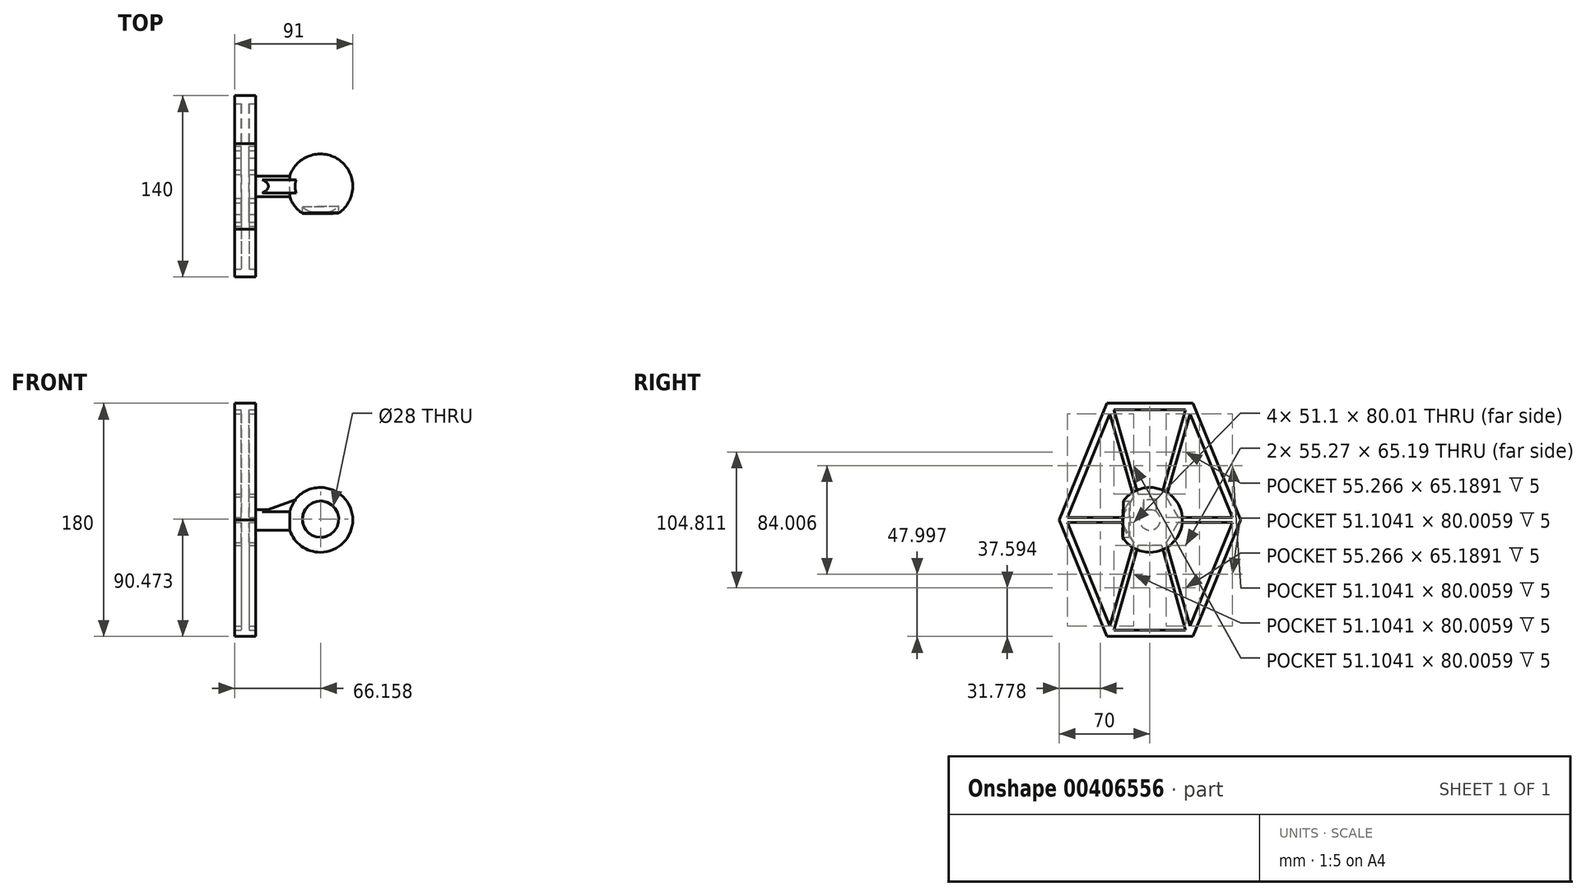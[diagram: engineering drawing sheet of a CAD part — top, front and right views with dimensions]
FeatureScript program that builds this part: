
annotation { "Feature Type Name" : "Feature", "Feature Type Description" : "" }
export const myFeature = defineFeature(function(context is Context, id is Id, definition is map)
    precondition{}
    {
        {
            var Q0;
            Q0=qCreatedBy(makeId("Front.planeOp"),FACE);
            var sketch = newSketch(context, id + "F0", { "sketchPlane" : qUnion([Q0])});
            skArc(sketch, "E0", {"start": v(0, -25) * mm, "mid": v(25, 0) * mm, "end": v(0, 25) * mm});
            skLineSegment(sketch, "E1", {"start": v(0, 25) * mm, "end": v(0, -25) * mm});
            skSolve(sketch);
        }
        {
            var Q0;
            Q0=qSketchRegion(id+"F0",true);
            var Q1;
            Q1=sQuery(id+"F0.wireOp",EDGE,"E1");
            revolve(context, id + "F1", {"entities" : qUnion([Q0]), "axis" : qUnion([Q1]), "revolveType" : RevolveType.FULL});
        }
        {
            var Q0;
            Q0=qCreatedBy(makeId("Front.planeOp"),FACE);
            var sketch = newSketch(context, id + "F2", { "sketchPlane" : qUnion([Q0])});
            skLineSegment(sketch, "E2.bottom", {"start": v(0, 0) * mm, "end": v(-55, 0) * mm});
            skLineSegment(sketch, "E2.top", {"start": v(0, 8) * mm, "end": v(-55, 8) * mm});
            skLineSegment(sketch, "E2.left", {"start": v(0, 0) * mm, "end": v(0, 8) * mm});
            skLineSegment(sketch, "E2.right", {"start": v(-55, 0) * mm, "end": v(-55, 8) * mm});
            skSolve(sketch);
        }
        {
            var Q0;
            Q0=qSketchRegion(id+"F2",true);
            var Q1;
            Q1=sQuery(id+"F2.wireOp",EDGE,"E2.bottom");
            revolve(context, id + "F3", {"operationType" : NewBodyOperationType.ADD, "entities" : qUnion([Q0]), "axis" : qUnion([Q1]), "revolveType" : RevolveType.FULL});
        }
        {
            var Q0;
            Q0=makeQuery(id+"F3.opRevolve","SWEPT_FACE",FACE,{"disambiguationData":[OSD([sQuery(id+"F2.wireOp",EDGE,"E2.right")])]});
            var sketch = newSketch(context, id + "F4", { "sketchPlane" : qUnion([Q0])});
            skLineSegment(sketch, "E3", {"start": v(0, 90) * mm, "end": v(-33.06, 90) * mm});
            skLineSegment(sketch, "E4", {"start": v(-33.06, 90) * mm, "end": v(-70, 0) * mm});
            skLineSegment(sketch, "E5", {"start": v(-70, 0) * mm, "end": v(0, 0) * mm, "construction": true});
            skLineSegment(sketch, "E6", {"start": v(0, 0) * mm, "end": v(0, 90) * mm, "construction": true});
            skLineSegment(sketch, "E7.MirrorCS", {"start": v(-33.06, -90) * mm, "end": v(-70, 0) * mm});
            skLineSegment(sketch, "E8.MirrorCS", {"start": v(0, -90) * mm, "end": v(-33.06, -90) * mm});
            skLineSegment(sketch, "E9.MirrorCS", {"start": v(0, 90) * mm, "end": v(33.06, 90) * mm});
            skLineSegment(sketch, "E10.MirrorCS", {"start": v(33.06, 90) * mm, "end": v(70, 0) * mm});
            skLineSegment(sketch, "E11.MirrorCS", {"start": v(33.06, -90) * mm, "end": v(70, 0) * mm});
            skLineSegment(sketch, "E12.MirrorCS", {"start": v(0, -90) * mm, "end": v(33.06, -90) * mm});
            skSolve(sketch);
        }
        {
            var Q0;
            Q0=qSketchRegion(id+"F4",true);
            extrude(context, id + "F5", {"entities" : qUnion([Q0]), "operationType" : NewBodyOperationType.ADD, "depth" : 6 * mm});
        }
        {
            var Q0;
            Q0=makeQuery(id+"F5.opExtrude","CAP_FACE",FACE,{"disambiguationData":[OSD([sQuery(id+"F4.wireOp",EDGE,"E3"),sQuery(id+"F4.wireOp",EDGE,"E4"),sQuery(id+"F4.wireOp",EDGE,"E7.MirrorCS"),sQuery(id+"F4.wireOp",EDGE,"E8.MirrorCS"),sQuery(id+"F4.wireOp",EDGE,"E9.MirrorCS"),sQuery(id+"F4.wireOp",EDGE,"E10.MirrorCS"),sQuery(id+"F4.wireOp",EDGE,"E11.MirrorCS"),sQuery(id+"F4.wireOp",EDGE,"E12.MirrorCS")])],"isStart":false});
            var sketch = newSketch(context, id + "F6", { "sketchPlane" : qUnion([Q0])});
            skLineSegment(sketch, "E13.0", {"start": v(-30.94, 82) * mm, "end": v(-12.67, 17.68) * mm});
            skLineSegment(sketch, "E14.0", {"start": v(-27.63, 85) * mm, "end": v(-9.12, 19.81) * mm});
            skLineSegment(sketch, "E15.0", {"start": v(-63.77, -2) * mm, "end": v(-21.72, -2) * mm});
            skLineSegment(sketch, "E16.0", {"start": v(-63.77, 2) * mm, "end": v(-21.72, 2) * mm});
            skLineSegment(sketch, "E17", {"start": v(0, 0) * mm, "end": v(0, -57.76) * mm, "construction": true});
            skLineSegment(sketch, "E18", {"start": v(0, 0) * mm, "end": v(92.77, 0) * mm, "construction": true});
            skLineSegment(sketch, "E19.MirrorCS", {"start": v(63.77, -2) * mm, "end": v(21.72, -2) * mm});
            skLineSegment(sketch, "E20.MirrorCS", {"start": v(63.77, 2) * mm, "end": v(21.72, 2) * mm});
            skLineSegment(sketch, "E21.MirrorCS", {"start": v(30.94, 82) * mm, "end": v(12.67, 17.68) * mm});
            skLineSegment(sketch, "E22.MirrorCS", {"start": v(27.63, 85) * mm, "end": v(9.12, 19.81) * mm});
            skLineSegment(sketch, "E23.MirrorCS", {"start": v(-30.94, -82) * mm, "end": v(-12.67, -17.68) * mm});
            skLineSegment(sketch, "E24.MirrorCS", {"start": v(-27.63, -85) * mm, "end": v(-9.12, -19.81) * mm});
            skLineSegment(sketch, "E25.MirrorCS", {"start": v(27.63, -85) * mm, "end": v(9.12, -19.81) * mm});
            skLineSegment(sketch, "E26.MirrorCS", {"start": v(30.94, -82) * mm, "end": v(12.67, -17.68) * mm});
            skLineSegment(sketch, "E27.0", {"start": v(-9.12, 19.81) * mm, "end": v(9.12, 19.81) * mm});
            skLineSegment(sketch, "E27.1", {"start": v(12.67, 17.68) * mm, "end": v(21.72, 2) * mm});
            skLineSegment(sketch, "E27.2", {"start": v(21.72, -2) * mm, "end": v(12.67, -17.68) * mm});
            skLineSegment(sketch, "E27.3", {"start": v(9.12, -19.81) * mm, "end": v(-9.12, -19.81) * mm});
            skLineSegment(sketch, "E27.4", {"start": v(-12.67, -17.68) * mm, "end": v(-21.72, -2) * mm});
            skLineSegment(sketch, "E27.5", {"start": v(-21.72, 2) * mm, "end": v(-12.67, 17.68) * mm});
            skPoint(sketch, "E27.0.midPoint", {"position": v(0, 19.81) * mm});
            skPoint(sketch, "E28.end.orphan", {"position": v(-10.36, 9.54) * mm});
            skPoint(sketch, "E28.start.orphan", {"position": v(-6.97, 12.24) * mm});
            skPoint(sketch, "E29.orphan", {"position": v(-11.44, 19.81) * mm});
            skPoint(sketch, "E30.end.orphan", {"position": v(6.97, 12.24) * mm});
            skPoint(sketch, "E30.start.orphan", {"position": v(10.36, 9.54) * mm});
            skPoint(sketch, "E31.orphan", {"position": v(11.44, 19.81) * mm});
            skPoint(sketch, "E32.orphan", {"position": v(14.09, 2) * mm});
            skPoint(sketch, "E33.MirrorCS.end.orphan", {"position": v(14.09, -2) * mm});
            skPoint(sketch, "E34.end.orphan", {"position": v(10.36, -9.54) * mm});
            skPoint(sketch, "E35.orphan", {"position": v(6.97, -12.24) * mm});
            skPoint(sketch, "E36.end.orphan", {"position": v(-6.97, -12.24) * mm});
            skPoint(sketch, "E36.start.orphan", {"position": v(-10.36, -9.54) * mm});
            skPoint(sketch, "E37.end.orphan", {"position": v(-14.09, -2) * mm});
            skPoint(sketch, "E37.start.orphan", {"position": v(-14.09, 2) * mm});
            skLineSegment(sketch, "E38.0", {"start": v(-33.06, 90) * mm, "end": v(-70, 0) * mm});
            skLineSegment(sketch, "E38.1", {"start": v(-33.06, -90) * mm, "end": v(33.06, -90) * mm});
            skLineSegment(sketch, "E38.2", {"start": v(33.06, -90) * mm, "end": v(70, 0) * mm});
            skLineSegment(sketch, "E38.3", {"start": v(-70, 0) * mm, "end": v(-33.06, -90) * mm});
            skLineSegment(sketch, "E38.4", {"start": v(70, 0) * mm, "end": v(33.06, 90) * mm});
            skLineSegment(sketch, "E38.5", {"start": v(33.06, 90) * mm, "end": v(-33.06, 90) * mm});
            skLineSegment(sketch, "E39.0", {"start": v(27.63, 85) * mm, "end": v(-27.63, 85) * mm});
            skLineSegment(sketch, "E39.1", {"start": v(-63.77, -2) * mm, "end": v(-30.94, -82) * mm});
            skLineSegment(sketch, "E39.2", {"start": v(-27.63, -85) * mm, "end": v(27.63, -85) * mm});
            skLineSegment(sketch, "E39.3", {"start": v(-30.94, 82) * mm, "end": v(-63.77, 2) * mm});
            skLineSegment(sketch, "E39.4", {"start": v(30.94, -82) * mm, "end": v(63.77, -2) * mm});
            skLineSegment(sketch, "E39.5", {"start": v(63.77, 2) * mm, "end": v(30.94, 82) * mm});
            skPoint(sketch, "E40.orphan", {"position": v(-31.64, 84.45) * mm});
            skPoint(sketch, "E41.orphan", {"position": v(-27.79, 85.55) * mm});
            skPoint(sketch, "E42.orphan", {"position": v(31.64, 84.45) * mm});
            skPoint(sketch, "E43.orphan", {"position": v(27.79, 85.55) * mm});
            skPoint(sketch, "E44.orphan", {"position": v(64.6, 2) * mm});
            skPoint(sketch, "E45.MirrorCS.end.orphan", {"position": v(64.6, -2) * mm});
            skPoint(sketch, "E46.orphan", {"position": v(31.64, -84.45) * mm});
            skPoint(sketch, "E47.orphan", {"position": v(27.79, -85.55) * mm});
            skPoint(sketch, "E48.orphan", {"position": v(-31.64, -84.45) * mm});
            skPoint(sketch, "E49.orphan", {"position": v(-27.79, -85.55) * mm});
            skPoint(sketch, "E50.orphan", {"position": v(-64.6, 2) * mm});
            skPoint(sketch, "E51.orphan", {"position": v(-64.6, -2) * mm});
            skSolve(sketch);
        }
        {
            var Q0;
            Q0=qSketchRegion(id+"F6",true);
            extrude(context, id + "F7", {"entities" : qUnion([Q0]), "operationType" : NewBodyOperationType.ADD, "depth" : 5 * mm, "hasSecondDirection" : true, "secondDirectionOppositeDirection" : true, "secondDirectionDepth" : 11 * mm});
        }
        {
            var Q0;
            Q0=qCreatedBy(makeId("Front.planeOp"),FACE);
            var sketch = newSketch(context, id + "F8", { "sketchPlane" : qUnion([Q0])});
            skLineSegment(sketch, "E52", {"start": v(-44.96, 6.15) * mm, "end": v(-11.83, 18.46) * mm});
            skLineSegment(sketch, "E53", {"start": v(-11.83, 18.46) * mm, "end": v(-11.83, 5.2) * mm});
            skLineSegment(sketch, "E54", {"start": v(-11.83, 5.2) * mm, "end": v(-44.96, 6.15) * mm});
            skSolve(sketch);
        }
        {
            var Q0;
            Q0=makeQuery(id+"F8.imprint","IMPRINT",FACE,{"disambiguationData":[TD([[makeQuery(id+"F8.imprint","IMPRINT",EDGE,{"derivedFrom":sQuery(id+"F8.wireOp",EDGE,"E52")}),-1.0]])]});
            extrude(context, id + "F9", {"entities" : qUnion([Q0]), "operationType" : NewBodyOperationType.ADD, "depth" : 5 * mm, "hasSecondDirection" : true, "secondDirectionOppositeDirection" : true, "secondDirectionDepth" : 5 * mm});
        }
        {
            var Q0;
            Q0=qCreatedBy(makeId("Front.planeOp"),FACE);
            var sketch = newSketch(context, id + "F10", { "sketchPlane" : qUnion([Q0])});
            skCircle(sketch, "E55", {"center": v(0.16, 0.47) * mm, "radius": 14 * mm});
            skSolve(sketch);
        }
        {
            var Q0;
            Q0=qSketchRegion(id+"F10",true);
            extrude(context, id + "F11", {"entities" : qUnion([Q0]), "operationType" : NewBodyOperationType.REMOVE, "depth" : 25 * mm});
        }
        {
            var Q0;
            Q0=qCreatedBy(makeId("Front.planeOp"),FACE);
            var sketch = newSketch(context, id + "F12", { "sketchPlane" : qUnion([Q0])});
            skArc(sketch, "E56", {"start": v(-0.15, -20.84) * mm, "mid": v(20.84, 0.16) * mm, "end": v(-0.15, 21.16) * mm});
            skLineSegment(sketch, "E57", {"start": v(-0.15, 21.16) * mm, "end": v(-0.15, -20.84) * mm});
            skSolve(sketch);
        }
        {
            var Q0;
            Q0=qSketchRegion(id+"F12",true);
            var Q1;
            Q1=sQuery(id+"F12.wireOp",EDGE,"E57");
            revolve(context, id + "F13", {"operationType" : NewBodyOperationType.ADD, "entities" : qUnion([Q0]), "axis" : qUnion([Q1]), "revolveType" : RevolveType.FULL});
        }
    });
